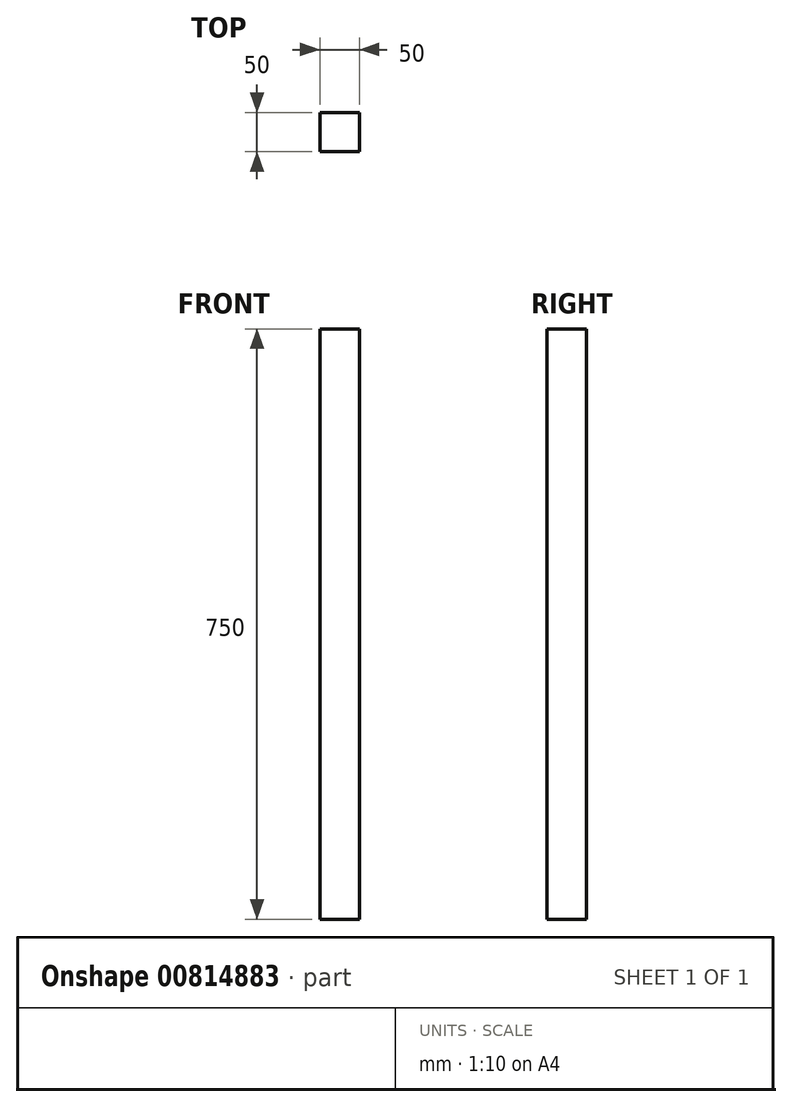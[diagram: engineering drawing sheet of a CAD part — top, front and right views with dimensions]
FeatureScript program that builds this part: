
annotation { "Feature Type Name" : "Feature", "Feature Type Description" : "" }
export const myFeature = defineFeature(function(context is Context, id is Id, definition is map)
    precondition{}
    {
        {
            var Q0;
            Q0=qCreatedBy(makeId("Front.planeOp"),FACE);
            var sketch = newSketch(context, id + "F0", { "sketchPlane" : qUnion([Q0])});
            skLineSegment(sketch, "E0", {"start": v(0, -200) * mm, "end": v(0, 550) * mm});
            skLineSegment(sketch, "E1", {"start": v(0, -200) * mm, "end": v(50, -200) * mm});
            skLineSegment(sketch, "E2", {"start": v(50, -200) * mm, "end": v(50, 550) * mm});
            skLineSegment(sketch, "E3", {"start": v(50, 550) * mm, "end": v(0, 550) * mm});
            skSolve(sketch);
        }
        {
            var Q0;
            Q0=makeQuery(id+"F0.imprint","IMPRINT",FACE,{"disambiguationData":[TD([[makeQuery(id+"F0.imprint","IMPRINT",EDGE,{"derivedFrom":sQuery(id+"F0.wireOp",EDGE,"E0")}),-1.0]])]});
            extrude(context, id + "F1", {"entities" : qUnion([Q0]), "oppositeDirection" : true, "depth" : 50 * mm, "offsetDistance" : 25 * mm});
        }
    });
